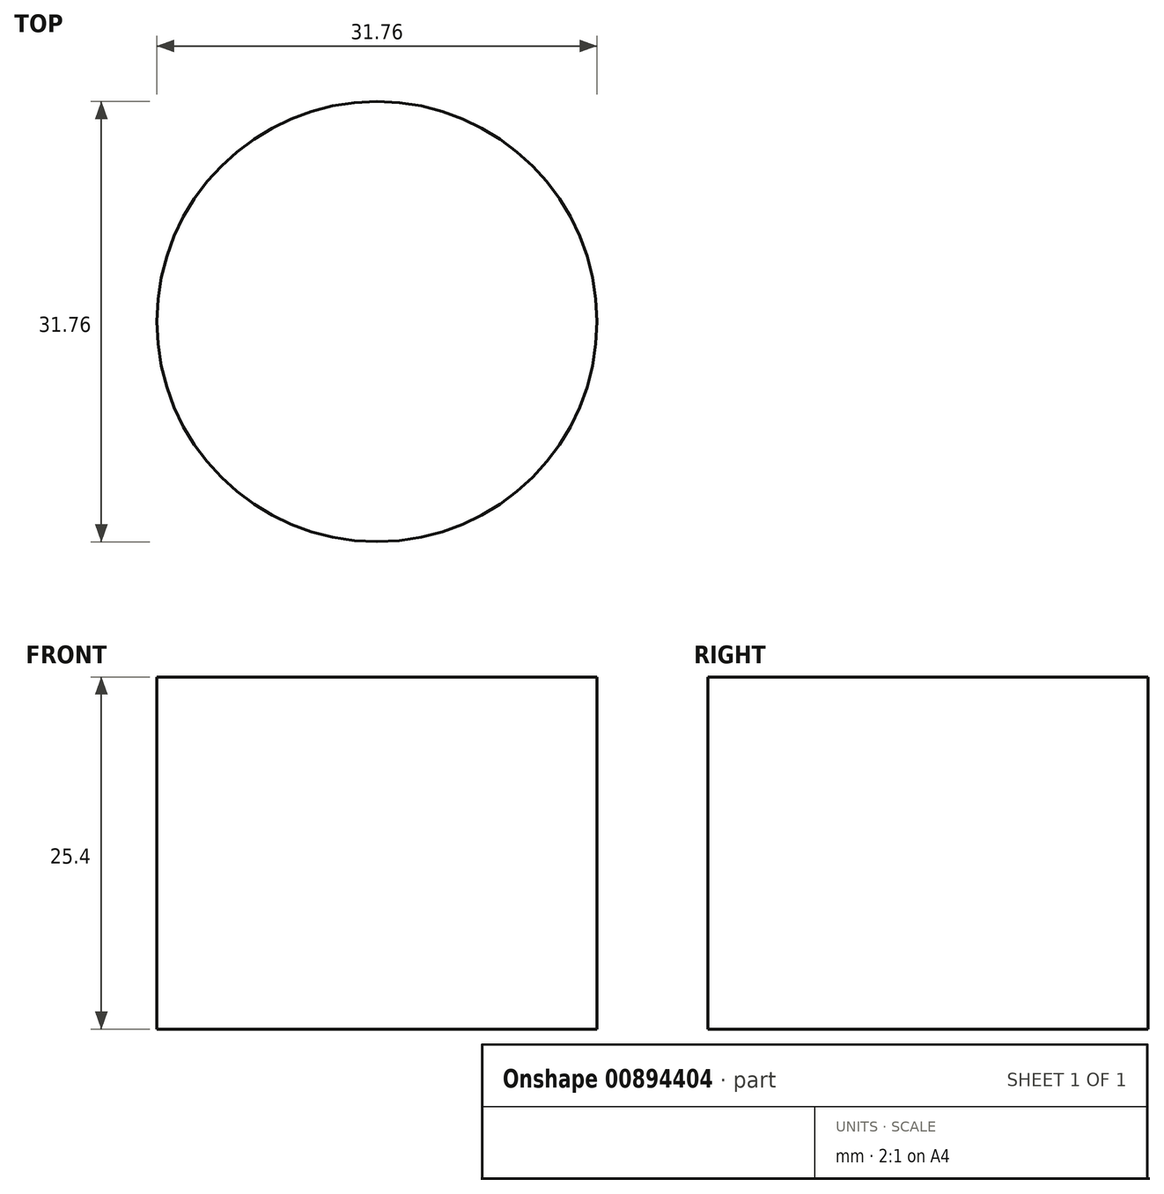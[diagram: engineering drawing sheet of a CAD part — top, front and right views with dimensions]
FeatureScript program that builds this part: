
annotation { "Feature Type Name" : "Feature", "Feature Type Description" : "" }
export const myFeature = defineFeature(function(context is Context, id is Id, definition is map)
    precondition{}
    {
        {
            var Q0;
            Q0=qCreatedBy(makeId("Top.planeOp"),FACE);
            var sketch = newSketch(context, id + "F0", { "sketchPlane" : qUnion([Q0])});
            skCircle(sketch, "E0", {"center": v(0, 0) * mm, "radius": 15.88 * mm});
            skSolve(sketch);
        }
        {
            var Q0;
            Q0 = qSketchRegion(id + "F0", true);
            extrude(context, id + "F1", {"entities" : qUnion([Q0]), "depth" : 25.4 * mm, "offsetDistance" : 25.4 * mm});
        }
    });
